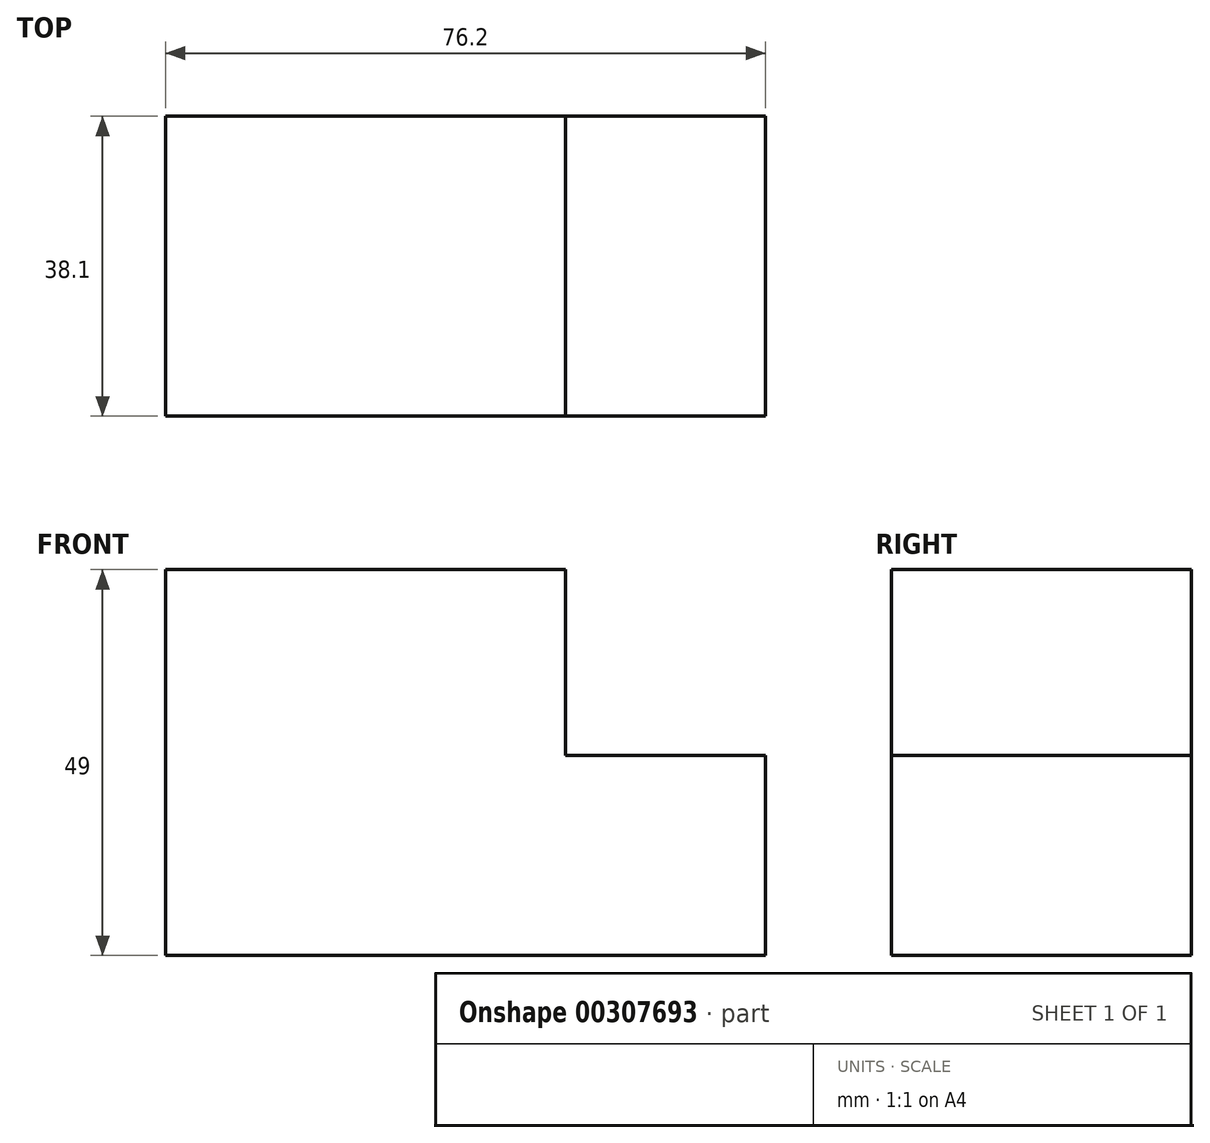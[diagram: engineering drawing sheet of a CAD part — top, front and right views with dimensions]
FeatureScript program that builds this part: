
annotation { "Feature Type Name" : "Feature", "Feature Type Description" : "" }
export const myFeature = defineFeature(function(context is Context, id is Id, definition is map)
    precondition{}
    {
        {
            var Q0;
            Q0=qCreatedBy(makeId("Front.planeOp"),FACE);
            var sketch = newSketch(context, id + "F0", { "sketchPlane" : qUnion([Q0])});
            skLineSegment(sketch, "E0", {"start": v(-35.78, -42.3) * mm, "end": v(40.42, -42.3) * mm});
            skLineSegment(sketch, "E1", {"start": v(40.42, -42.3) * mm, "end": v(40.42, -16.9) * mm});
            skLineSegment(sketch, "E2", {"start": v(40.42, -16.9) * mm, "end": v(15.02, -16.9) * mm});
            skLineSegment(sketch, "E3", {"start": v(15.02, -16.9) * mm, "end": v(15.02, 6.7) * mm});
            skLineSegment(sketch, "E4", {"start": v(15.02, 6.7) * mm, "end": v(-35.78, 6.7) * mm});
            skLineSegment(sketch, "E5", {"start": v(-35.78, 6.7) * mm, "end": v(-35.78, -42.3) * mm});
            skSolve(sketch);
        }
        {
            var Q0;
            Q0=makeQuery(id+"F0.imprint","IMPRINT",FACE,{"disambiguationData":[TD([[makeQuery(id+"F0.imprint","IMPRINT",EDGE,{"derivedFrom":sQuery(id+"F0.wireOp",EDGE,"E0")}),1.0]])]});
            extrude(context, id + "F1", {"entities" : qUnion([Q0]), "depth" : 38.1 * mm});
        }
    });
